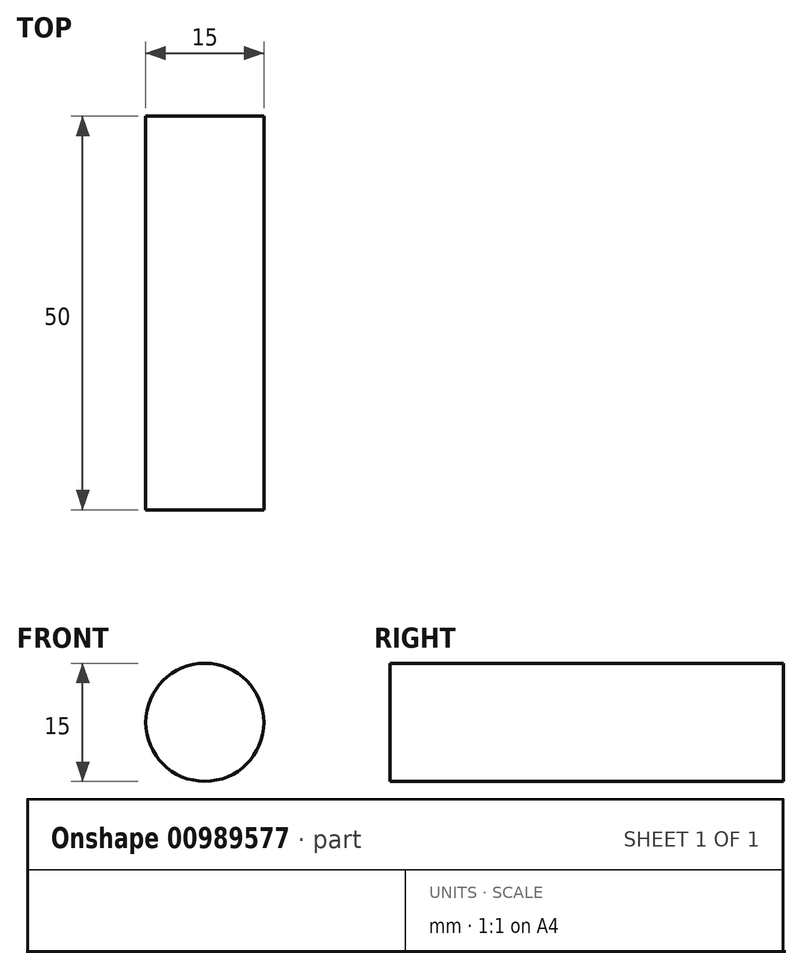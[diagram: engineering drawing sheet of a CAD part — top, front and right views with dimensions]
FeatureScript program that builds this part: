
annotation { "Feature Type Name" : "Feature", "Feature Type Description" : "" }
export const myFeature = defineFeature(function(context is Context, id is Id, definition is map)
    precondition{}
    {
        {
            var Q0;
            Q0=qCreatedBy(makeId("Front.planeOp"),FACE);
            var sketch = newSketch(context, id + "F0", { "sketchPlane" : qUnion([Q0])});
            skCircle(sketch, "E0", {"center": v(0, 0) * mm, "radius": 7.5 * mm});
            skSolve(sketch);
        }
        {
            var Q0;
            Q0 = qSketchRegion(id + "F0", true);
            extrude(context, id + "F1", {"entities" : qUnion([Q0]), "oppositeDirection" : true, "depth" : 50 * mm, "offsetDistance" : 25 * mm});
        }
    });
